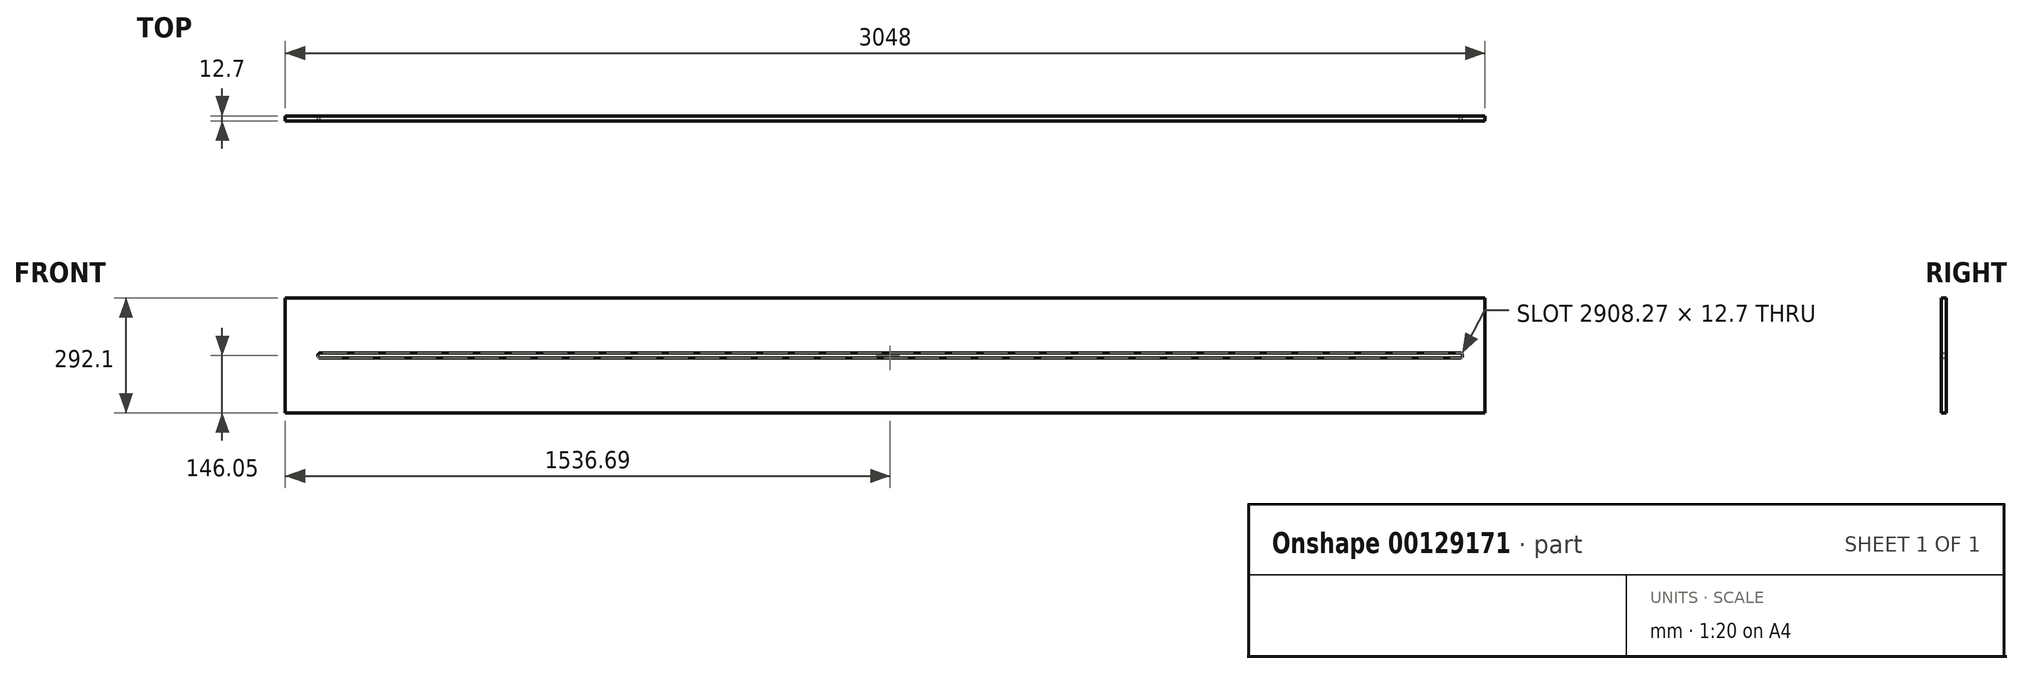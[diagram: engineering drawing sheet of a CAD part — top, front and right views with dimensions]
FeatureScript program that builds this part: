
annotation { "Feature Type Name" : "Feature", "Feature Type Description" : "" }
export const myFeature = defineFeature(function(context is Context, id is Id, definition is map)
    precondition{}
    {
        {
            var Q0;
            Q0=qCreatedBy(makeId("Front.planeOp"),FACE);
            var sketch = newSketch(context, id + "F0", { "sketchPlane" : qUnion([Q0])});
            skLineSegment(sketch, "E0.bottom", {"start": v(-1524, 146.05) * mm, "end": v(1524, 146.05) * mm});
            skLineSegment(sketch, "E0.top", {"start": v(-1524, -146.05) * mm, "end": v(1524, -146.05) * mm});
            skLineSegment(sketch, "E0.left", {"start": v(-1524, 146.05) * mm, "end": v(-1524, -146.05) * mm});
            skLineSegment(sketch, "E0.right", {"start": v(1524, 146.05) * mm, "end": v(1524, -146.05) * mm});
            skPoint(sketch, "E0.middle", {"position": v(0, 0) * mm});
            skLineSegment(sketch, "E1", {"start": v(-1524, 0) * mm, "end": v(1524, 0) * mm});
            skArc(sketch, "E2", {"start": v(-1435.1, 6.35) * mm, "mid": v(-1441.45, -0.08) * mm, "end": v(-1434.95, -6.35) * mm});
            skArc(sketch, "E3", {"start": v(1460.5, -6.35) * mm, "mid": v(1466.82, 0.61) * mm, "end": v(1459.28, 6.23) * mm});
            skLineSegment(sketch, "E4", {"start": v(1459.28, 6.23) * mm, "end": v(-1435.1, 6.35) * mm});
            skLineSegment(sketch, "E5", {"start": v(-1435.25, -6.35) * mm, "end": v(1460.5, -6.35) * mm});
            skSolve(sketch);
        }
        {
            var Q0;
            {var subQ6=sQuery(id+"F0.wireOp",EDGE,"E0.bottom");Q0=makeQuery(id+"F0.imprint","IMPRINT",FACE,{"disambiguationData":[TD([[makeQuery(id+"F0.imprint","IMPRINT",EDGE,{"derivedFrom":subQ6}),-1.0]])]});}
            var Q1;
            {var subQ10=sQuery(id+"F0.wireOp",EDGE,"E0.top");Q1=makeQuery(id+"F0.imprint","IMPRINT",FACE,{"disambiguationData":[TD([[makeQuery(id+"F0.imprint","IMPRINT",EDGE,{"derivedFrom":subQ10}),1.0]])]});}
            extrude(context, id + "F1", {"entities" : qUnion([Q0, Q1]), "depth" : 12.7 * mm});
        }
    });
